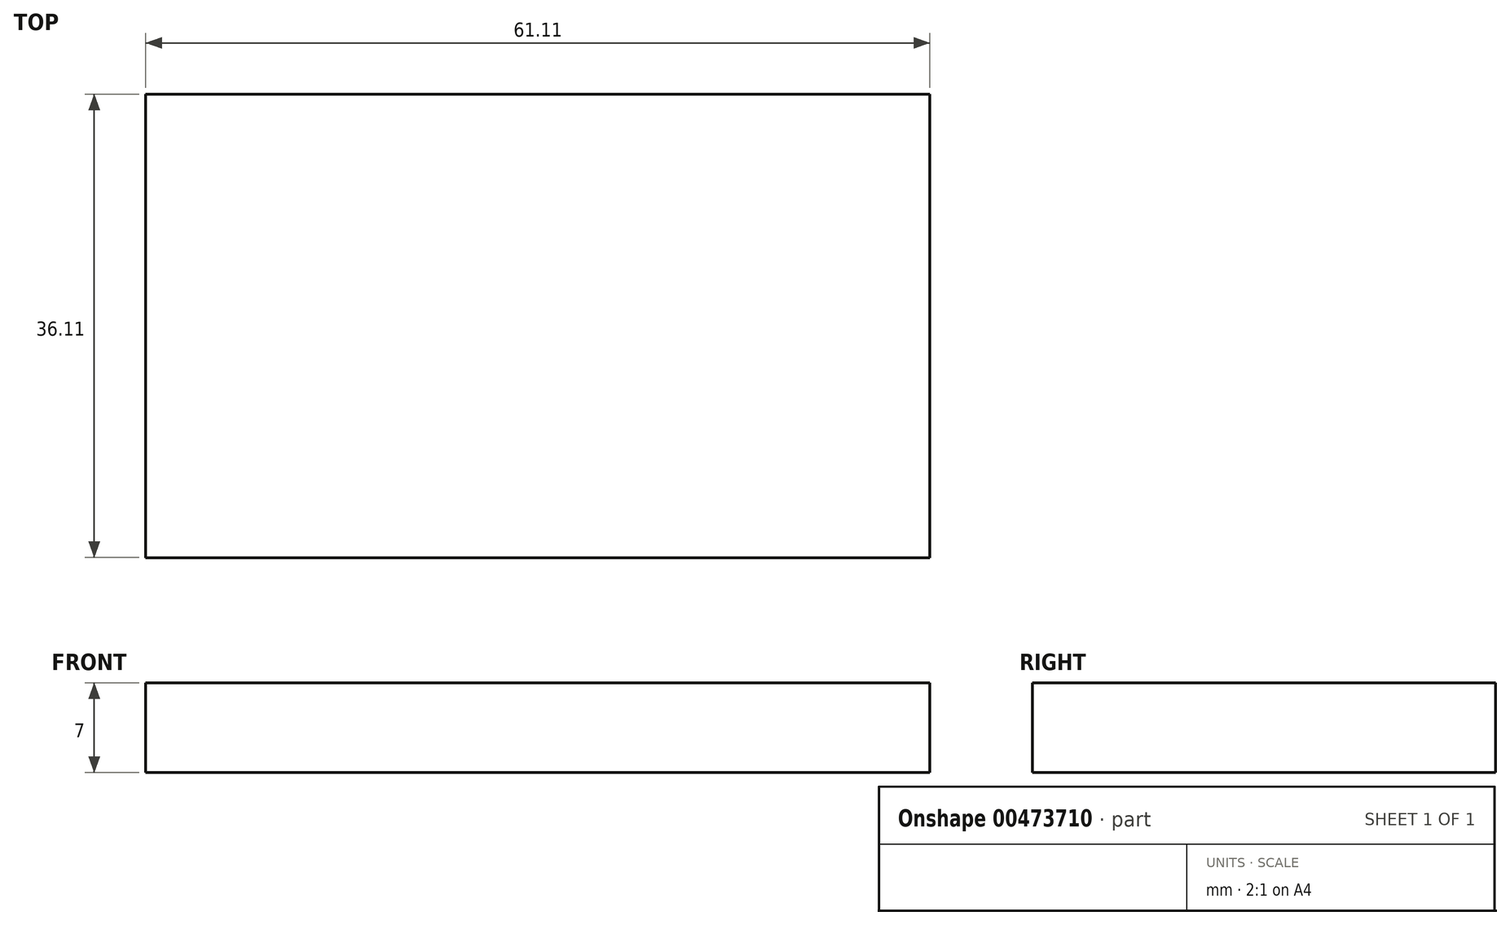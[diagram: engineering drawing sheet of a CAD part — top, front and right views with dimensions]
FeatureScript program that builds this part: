
annotation { "Feature Type Name" : "Feature", "Feature Type Description" : "" }
export const myFeature = defineFeature(function(context is Context, id is Id, definition is map)
    precondition{}
    {
        {
            var Q0;
            Q0=qCreatedBy(makeId("Top.planeOp"),FACE);
            var sketch = newSketch(context, id + "F0", { "sketchPlane" : qUnion([Q0])});
            skLineSegment(sketch, "E0.bottom", {"start": v(-33.45, 16.38) * mm, "end": v(27.66, 16.38) * mm});
            skLineSegment(sketch, "E0.top", {"start": v(-33.45, -19.73) * mm, "end": v(27.66, -19.73) * mm});
            skLineSegment(sketch, "E0.left", {"start": v(-33.45, 16.38) * mm, "end": v(-33.45, -19.73) * mm});
            skLineSegment(sketch, "E0.right", {"start": v(27.66, 16.38) * mm, "end": v(27.66, -19.73) * mm});
            skSolve(sketch);
        }
        {
            var Q0;
            Q0 = qSketchRegion(id + "F0", true);
            extrude(context, id + "F1", {"entities" : qUnion([Q0]), "depth" : 7 * mm});
        }
    });
